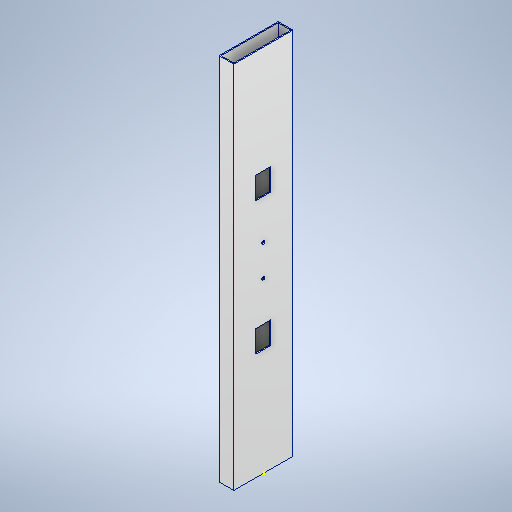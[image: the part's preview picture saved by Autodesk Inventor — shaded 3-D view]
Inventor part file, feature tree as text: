
AUTODESK INVENTOR PART (.ipt)
format: ipt  version: 2025 (Build 290162000, 162)  size: 309,760 bytes
history: native  units: mm
features: sketch x7, extrude x4
ambient origin geometry x8: Origin, YZ Plane, XZ Plane, XY Plane, X Axis, Y Axis, Z Axis, Center Point
bodies: Body1 (feature_tree)
feature tree (11):
  extrude  "Wyciągnięcie proste2"  Depth=20.0mm
  extrude  "Wyciągnięcie proste3"  Depth=80.0mm
  sketch  "Szkic4"
  sketch  "Szkic5"
  sketch  "Szkic6"
  extrude  "Wyciągnięcie proste4"  Depth=1.4mm
  extrude  "Wyciągnięcie proste5"  Depth=1.4mm
  sketch  "Szkic2"
  sketch  "Szkic3"
  sketch  "Szkic7"
  sketch  "Szkic8"
